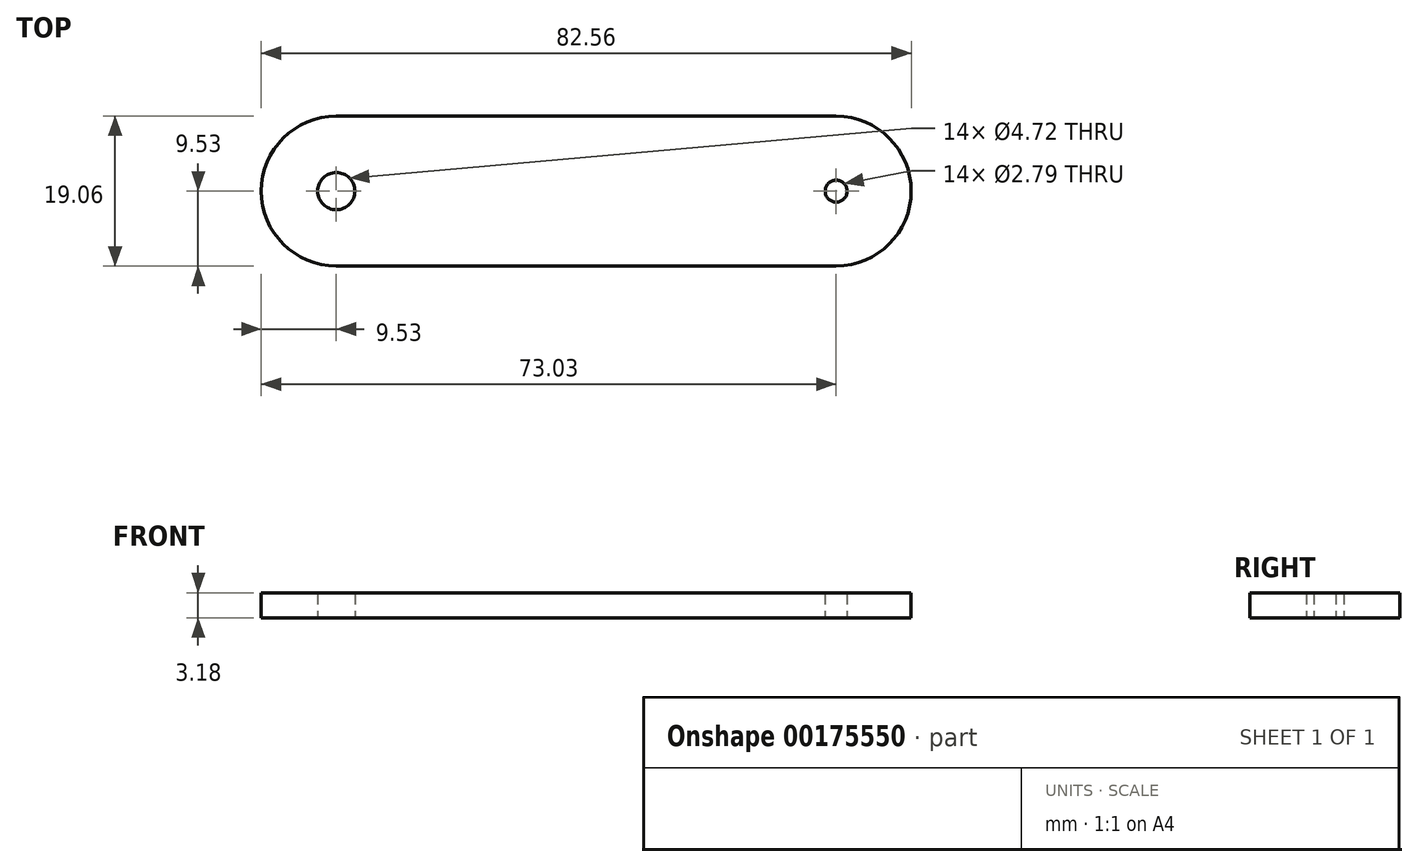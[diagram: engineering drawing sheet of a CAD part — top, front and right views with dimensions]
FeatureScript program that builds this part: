
annotation { "Feature Type Name" : "Feature", "Feature Type Description" : "" }
export const myFeature = defineFeature(function(context is Context, id is Id, definition is map)
    precondition{}
    {
        {
            var Q0;
            Q0=qCreatedBy(makeId("Top.planeOp"),FACE);
            var sketch = newSketch(context, id + "F0", { "sketchPlane" : qUnion([Q0])});
            skLineSegment(sketch, "E0.bottom", {"start": v(63.5, 9.53) * mm, "end": v(0, 9.53) * mm});
            skLineSegment(sketch, "E0.top", {"start": v(63.5, -9.53) * mm, "end": v(0, -9.53) * mm});
            skArc(sketch, "E1", {"start": v(0, 9.53) * mm, "mid": v(-9.53, 0) * mm, "end": v(0, -9.53) * mm});
            skArc(sketch, "E2", {"start": v(63.5, -9.53) * mm, "mid": v(73.03, 0) * mm, "end": v(63.5, 9.53) * mm});
            skCircle(sketch, "E3", {"center": v(0, 0) * mm, "radius": 2.36 * mm});
            skCircle(sketch, "E4", {"center": v(63.5, 0) * mm, "radius": 1.4 * mm});
            skSolve(sketch);
        }
        {
            var Q0;
            Q0 = qSketchRegion(id + "F0", true);
            extrude(context, id + "F1", {"entities" : qUnion([Q0]), "depth" : 3.17 * mm});
        }
    });
